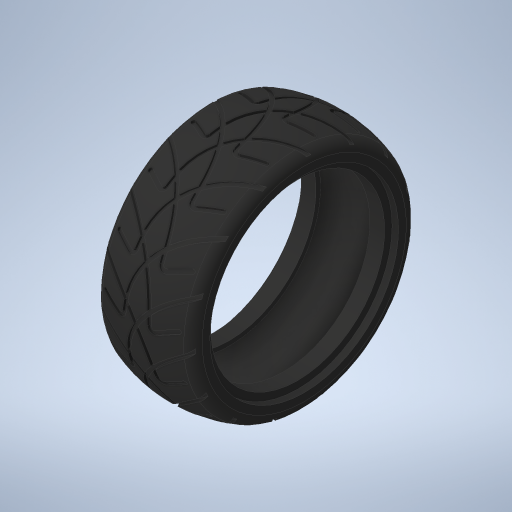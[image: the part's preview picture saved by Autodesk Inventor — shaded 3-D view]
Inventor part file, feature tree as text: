
AUTODESK INVENTOR PART (.ipt)
format: ipt  version: 2023.1 (Build 271208000, 208)  size: 1,800,192 bytes
history: native  units: in
note: dims shown in document units (in); Inventor stores cm internally (conversion verified against a paired STEP export)
features: sketch x3, revolve x2, fillet x1, plane x1, extrude x1, pattern_circular x1, mirror x1, other x1, projected_geometry x1
ambient origin geometry x8: Origin, YZ Plane, XZ Plane, XY Plane, X Axis, Y Axis, Z Axis, Center Point
bodies: Solid1 (feature_tree)
feature tree (12):
  revolve  "Revolution1"  [1 undecoded]
  fillet  "Fillet1"  Radius=0.23in
  plane  "Work Plane1"
  extrude  "Extrusion1"  Depth=2.6in
  pattern_circular  "Circular Pattern1"  [2 undecoded]
  mirror  "Mirror1"
  sketch  "Sketch1"  dims[d0=1.885in d1=0.07in d2=0.23in]
  sketch  "Sketch2"  dims[d3=2.045in d4=2.6in]
  other  "Srf1"
  sketch  "Sketch4"  dims[d5=1.045in d6=0.05in d7=90.0deg d8=0.125in d9=0.0297in d10=90.0deg d11=1.375in d12=0.8744in d13=0.3268in d14=0.765in d15=0.2455in d16=0.0625in d17=0.1044in d18=0.0415in d19=0.1248in d20=0.2825in d21=1.0in d22=0.0in d23=5.9055in d24=360.0deg]
  revolve  "RevolutionSrf1"  Angle=90.0deg
  projected_geometry  "Project Cut Edges1"
note: 3 required parameter values undecoded (feature->parameter linkage not recoverable at this tier; creation-order binding heuristic only, values carry confidence <= 0.55)